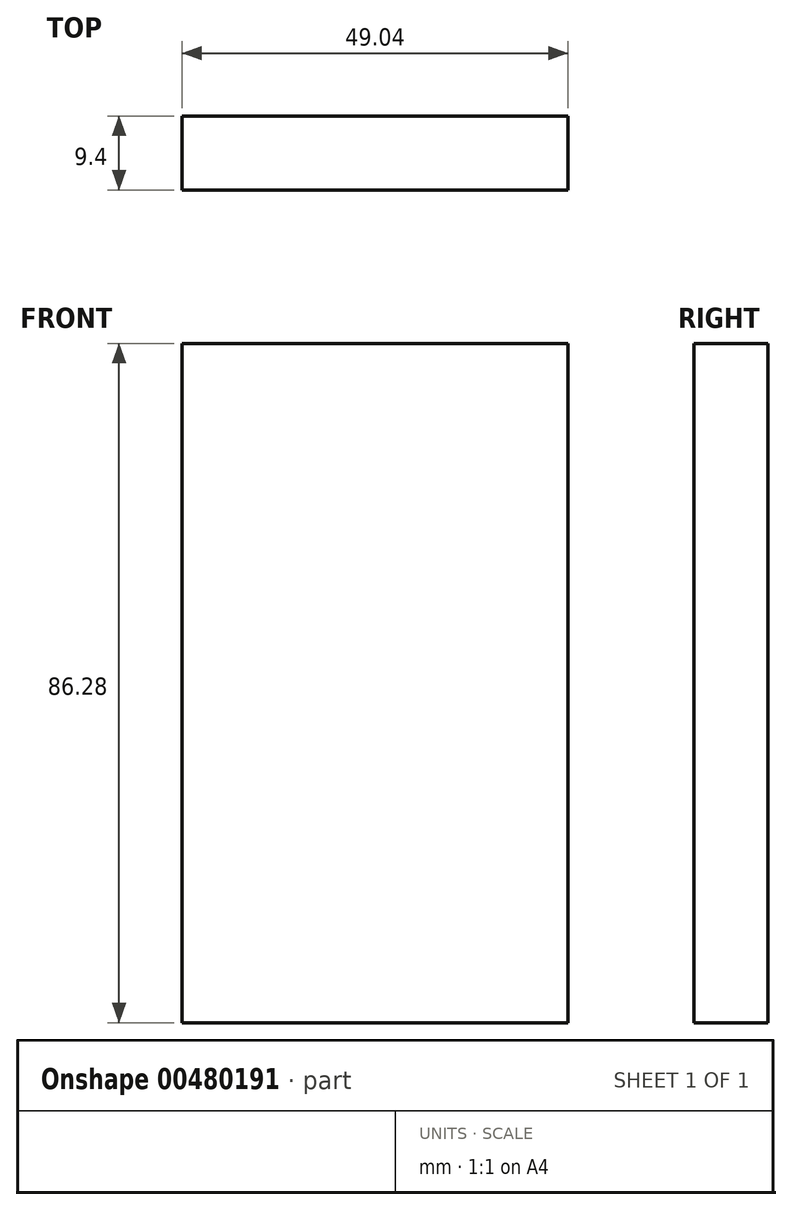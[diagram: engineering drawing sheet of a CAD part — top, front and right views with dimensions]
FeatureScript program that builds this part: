
annotation { "Feature Type Name" : "Feature", "Feature Type Description" : "" }
export const myFeature = defineFeature(function(context is Context, id is Id, definition is map)
    precondition{}
    {
        {
            var Q0;
            Q0=qCreatedBy(makeId("Front.planeOp"),FACE);
            var sketch = newSketch(context, id + "F0", { "sketchPlane" : qUnion([Q0])});
            skLineSegment(sketch, "E0.bottom", {"start": v(-37.8, 52.17) * mm, "end": v(11.25, 52.17) * mm});
            skLineSegment(sketch, "E0.top", {"start": v(-37.8, -34.1) * mm, "end": v(11.25, -34.1) * mm});
            skLineSegment(sketch, "E0.left", {"start": v(-37.8, 52.17) * mm, "end": v(-37.8, -34.1) * mm});
            skLineSegment(sketch, "E0.right", {"start": v(11.25, 52.17) * mm, "end": v(11.25, -34.1) * mm});
            skSolve(sketch);
        }
        {
            var Q0;
            Q0=makeQuery(id+"F0.imprint","IMPRINT",FACE,{"disambiguationData":[TD([[makeQuery(id+"F0.imprint","IMPRINT",EDGE,{"derivedFrom":sQuery(id+"F0.wireOp",EDGE,"E0.bottom")}),-1.0]])]});
            extrude(context, id + "F1", {"entities" : qUnion([Q0]), "depth" : 9.4 * mm});
        }
    });
